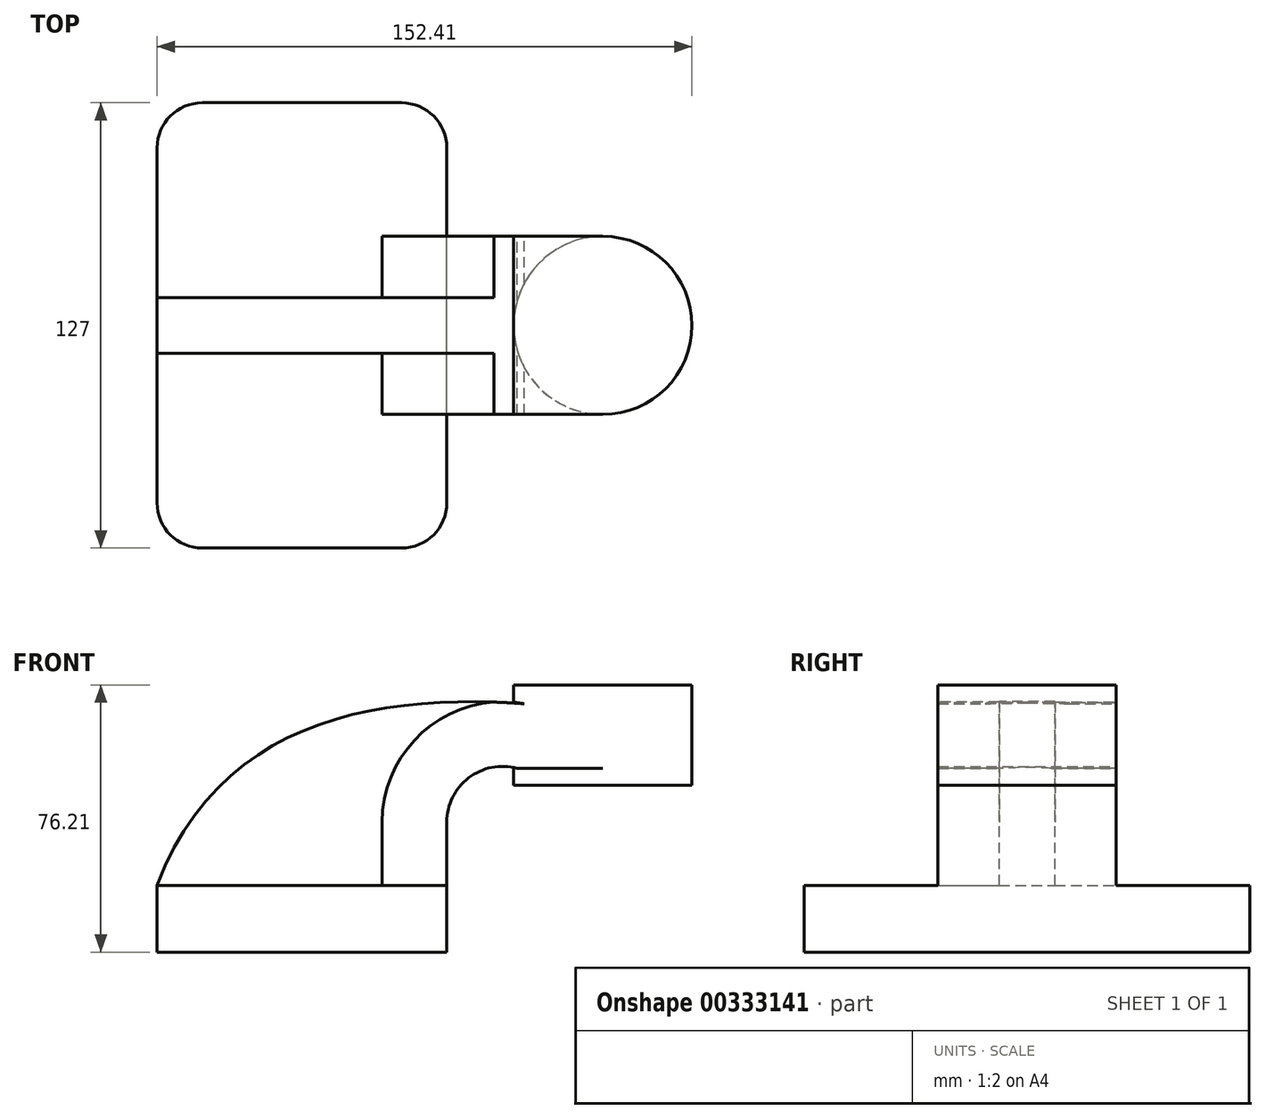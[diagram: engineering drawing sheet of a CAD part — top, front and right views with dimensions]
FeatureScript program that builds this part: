
annotation { "Feature Type Name" : "Feature", "Feature Type Description" : "" }
export const myFeature = defineFeature(function(context is Context, id is Id, definition is map)
    precondition{}
    {
        {
            var Q0;
            Q0=qCreatedBy(makeId("Front.planeOp"),FACE);
            var sketch = newSketch(context, id + "F0", { "sketchPlane" : qUnion([Q0])});
            skLineSegment(sketch, "E0.bottom", {"start": v(-41.28, 9.52) * mm, "end": v(41.28, 9.53) * mm});
            skLineSegment(sketch, "E0.top", {"start": v(-41.28, -9.53) * mm, "end": v(41.28, -9.53) * mm});
            skLineSegment(sketch, "E0.left", {"start": v(-41.28, 9.52) * mm, "end": v(-41.28, -9.53) * mm});
            skLineSegment(sketch, "E0.right", {"start": v(41.28, 9.53) * mm, "end": v(41.28, -9.52) * mm});
            skPoint(sketch, "E0.middle", {"position": v(0, 0) * mm});
            skLineSegment(sketch, "E1.bottom", {"start": v(60.32, 38.1) * mm, "end": v(111.12, 38.1) * mm});
            skLineSegment(sketch, "E1.top", {"start": v(60.32, 66.68) * mm, "end": v(111.12, 66.68) * mm});
            skLineSegment(sketch, "E1.left", {"start": v(60.32, 38.1) * mm, "end": v(60.32, 66.68) * mm});
            skLineSegment(sketch, "E1.right", {"start": v(111.12, 38.1) * mm, "end": v(111.12, 66.68) * mm});
            skPoint(sketch, "E1.middle", {"position": v(85.72, 52.39) * mm});
            skLineSegment(sketch, "E2", {"start": v(41.27, 9.53) * mm, "end": v(41.27, 27.55) * mm});
            skArc(sketch, "E3", {"start": v(41.27, 27.55) * mm, "mid": v(47.5, 40.17) * mm, "end": v(61.3, 42.88) * mm});
            skLineSegment(sketch, "E4", {"start": v(61.3, 42.88) * mm, "end": v(85.72, 42.88) * mm});
            skLineSegment(sketch, "E5.0", {"start": v(63.3, 61.3) * mm, "end": v(83.65, 61.3) * mm});
            skArc(sketch, "E5.1", {"start": v(22.86, 27.55) * mm, "mid": v(35.18, 53.88) * mm, "end": v(63.3, 61.3) * mm});
            skLineSegment(sketch, "E5.2", {"start": v(22.86, 9.53) * mm, "end": v(22.86, 27.55) * mm});
            skFitSpline(sketch, "E6", {"points": [v(-41.28, 9.52) * mm, v(63.3, 61.3) * mm], "startDerivative": vector(53.39, 141.42) * mm, "endDerivative": vector(126.21, -9.15) * mm});
            skPoint(sketch, "E7", {"position": v(85.72, 38.1) * mm});
            skLineSegment(sketch, "E8", {"start": v(85.72, 66.68) * mm, "end": v(85.72, 38.1) * mm});
            skSolve(sketch);
        }
        {
            var Q0;
            Q0=makeQuery(id+"F0.imprint","IMPRINT",FACE,{"disambiguationData":[TD([[makeQuery(id+"F0.imprint","IMPRINT",EDGE,{"derivedFrom":sQuery(id+"F0.wireOp",EDGE,"E0.top")}),1.0]])]});
            extrude(context, id + "F1", {"entities" : qUnion([Q0]), "endBound" : BoundingType.SYMMETRIC, "depth" : 127 * mm});
        }
        {
            var Q0;
            {var subQ0=sQuery(id+"F0.wireOp",EDGE,"E2");Q0=makeQuery(id+"F0.imprint","IMPRINT",FACE,{"disambiguationData":[TD([[makeQuery(id+"F0.imprint","IMPRINT",EDGE,{"derivedFrom":subQ0}),1.0]])]});}
            var Q1;
            {var subQ1=sQuery(id+"F0.wireOp",EDGE,"E4");Q1=makeQuery(id+"F0.imprint","IMPRINT",FACE,{"disambiguationData":[TD([[makeQuery(id+"F0.imprint","IMPRINT",EDGE,{"derivedFrom":subQ1}),1.0]])]});}
            extrude(context, id + "F2", {"entities" : qUnion([Q0, Q1]), "operationType" : NewBodyOperationType.ADD, "endBound" : BoundingType.SYMMETRIC, "depth" : 50.8 * mm});
        }
        {
            var Q0;
            {var subQ3=sQuery(id+"F0.wireOp",EDGE,"E5.2");Q0=makeQuery(id+"F0.imprint","IMPRINT",FACE,{"disambiguationData":[TD([[makeQuery(id+"F0.imprint","IMPRINT",EDGE,{"derivedFrom":subQ3}),1.0]])]});}
            extrude(context, id + "F3", {"entities" : qUnion([Q0]), "operationType" : NewBodyOperationType.ADD, "endBound" : BoundingType.SYMMETRIC, "depth" : 15.88 * mm});
        }
        {
            var Q0;
            {var subQ4=sQuery(id+"F0.wireOp",EDGE,"E1.right");Q0=makeQuery(id+"F0.imprint","IMPRINT",FACE,{"disambiguationData":[TD([[makeQuery(id+"F0.imprint","IMPRINT",EDGE,{"derivedFrom":subQ4}),1.0]])]});}
            var Q1;
            Q1=sQuery(id+"F0.wireOp",EDGE,"E8");
            revolve(context, id + "F4", {"operationType" : NewBodyOperationType.ADD, "entities" : qUnion([Q0]), "axis" : qUnion([Q1]), "revolveType" : RevolveType.FULL});
        }
        {
            var Q0;
            Q0=makeQuery(id+"F1.opExtrude","CAP_EDGE",EDGE,{"disambiguationData":[OSD([sQuery(id+"F0.wireOp",EDGE,"E0.right")])],"isStart":false});
            var Q1;
            Q1=makeQuery(id+"F1.opExtrude","CAP_EDGE",EDGE,{"disambiguationData":[OSD([sQuery(id+"F0.wireOp",EDGE,"E0.left")])],"isStart":false});
            var Q2;
            Q2=makeQuery(id+"F1.opExtrude","CAP_EDGE",EDGE,{"disambiguationData":[OSD([sQuery(id+"F0.wireOp",EDGE,"E0.left")])],"isStart":true});
            var Q3;
            Q3=makeQuery(id+"F1.opExtrude","CAP_EDGE",EDGE,{"disambiguationData":[OSD([sQuery(id+"F0.wireOp",EDGE,"E0.right")])],"isStart":true});
            fillet(context, id + "F5", {"entities" : qUnion([Q0, Q1, Q2, Q3]), "radius" : 12.88 * mm, "tangentPropagation" : true, "allowEdgeOverflow" : false});
        }
    });
